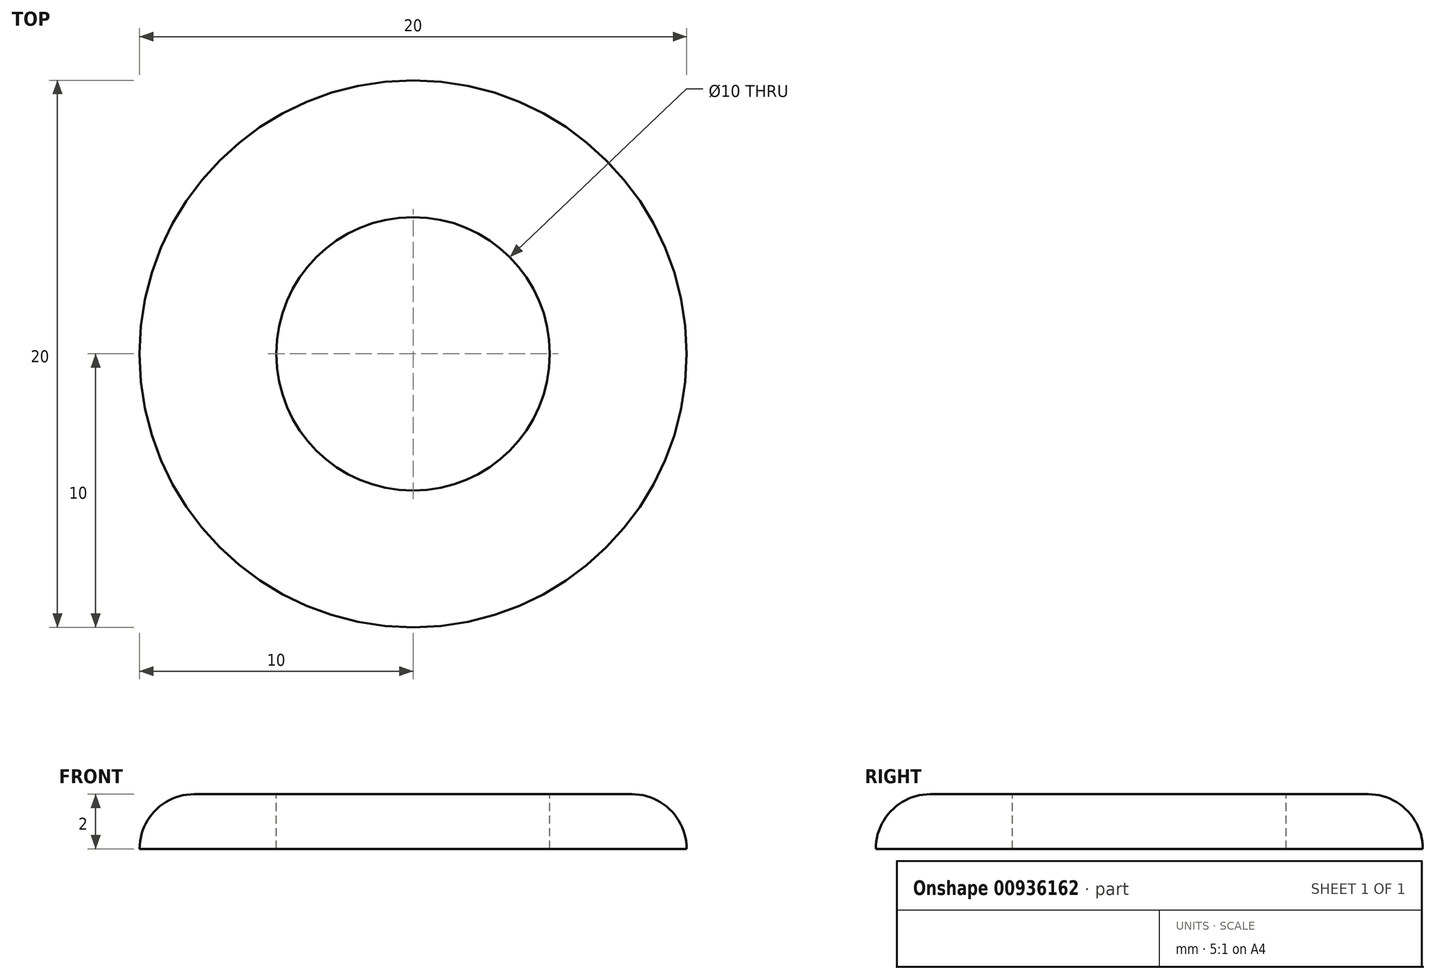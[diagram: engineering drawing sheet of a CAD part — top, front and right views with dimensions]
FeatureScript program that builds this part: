
annotation { "Feature Type Name" : "Feature", "Feature Type Description" : "" }
export const myFeature = defineFeature(function(context is Context, id is Id, definition is map)
    precondition{}
    {
        {
            var Q0;
            Q0=qCreatedBy(makeId("Top.planeOp"),FACE);
            var sketch = newSketch(context, id + "F0", { "sketchPlane" : qUnion([Q0])});
            skCircle(sketch, "E0", {"center": v(0, 0) * mm, "radius": 10 * mm});
            skSolve(sketch);
        }
        {
            var Q0;
            Q0 = qSketchRegion(id + "F0", true);
            extrude(context, id + "F1", {"entities" : qUnion([Q0]), "oppositeDirection" : true, "depth" : 2 * mm, "offsetDistance" : 25 * mm});
        }
        {
            var Q0;
            Q0=makeQuery(id+"F1.opExtrude","CAP_EDGE",EDGE,{"disambiguationData":[OSD([sQuery(id+"F0.wireOp",EDGE,"E0")])],"isStart":true});
            fillet(context, id + "F2", {"entities" : qUnion([Q0]), "radius" : 2 * mm, "tangentPropagation" : true, "allowEdgeOverflow" : false});
        }
        {
            var Q0;
            Q0=makeQuery(id+"F1.opExtrude","CAP_FACE",FACE,{"disambiguationData":[OSD([sQuery(id+"F0.wireOp",EDGE,"E0")])],"isStart":true});
            var sketch = newSketch(context, id + "F3", { "sketchPlane" : qUnion([Q0])});
            skCircle(sketch, "E1", {"center": v(0, 0) * mm, "radius": 5 * mm});
            skSolve(sketch);
        }
        {
            var Q0;
            Q0 = qSketchRegion(id + "F3", true);
            var Q1;
            Q1=makeQuery(id+"F3.imprint","IMPRINT",FACE,{"disambiguationData":[TD([[makeQuery(id+"F3.imprint","IMPRINT",EDGE,{"derivedFrom":sQuery(id+"F3.wireOp",EDGE,"E1")}),1.0]])]});
            extrude(context, id + "F4", {"entities" : qUnion([Q0, Q1]), "operationType" : NewBodyOperationType.REMOVE, "oppositeDirection" : true, "depth" : 25 * mm, "offsetDistance" : 25 * mm});
        }
    });
